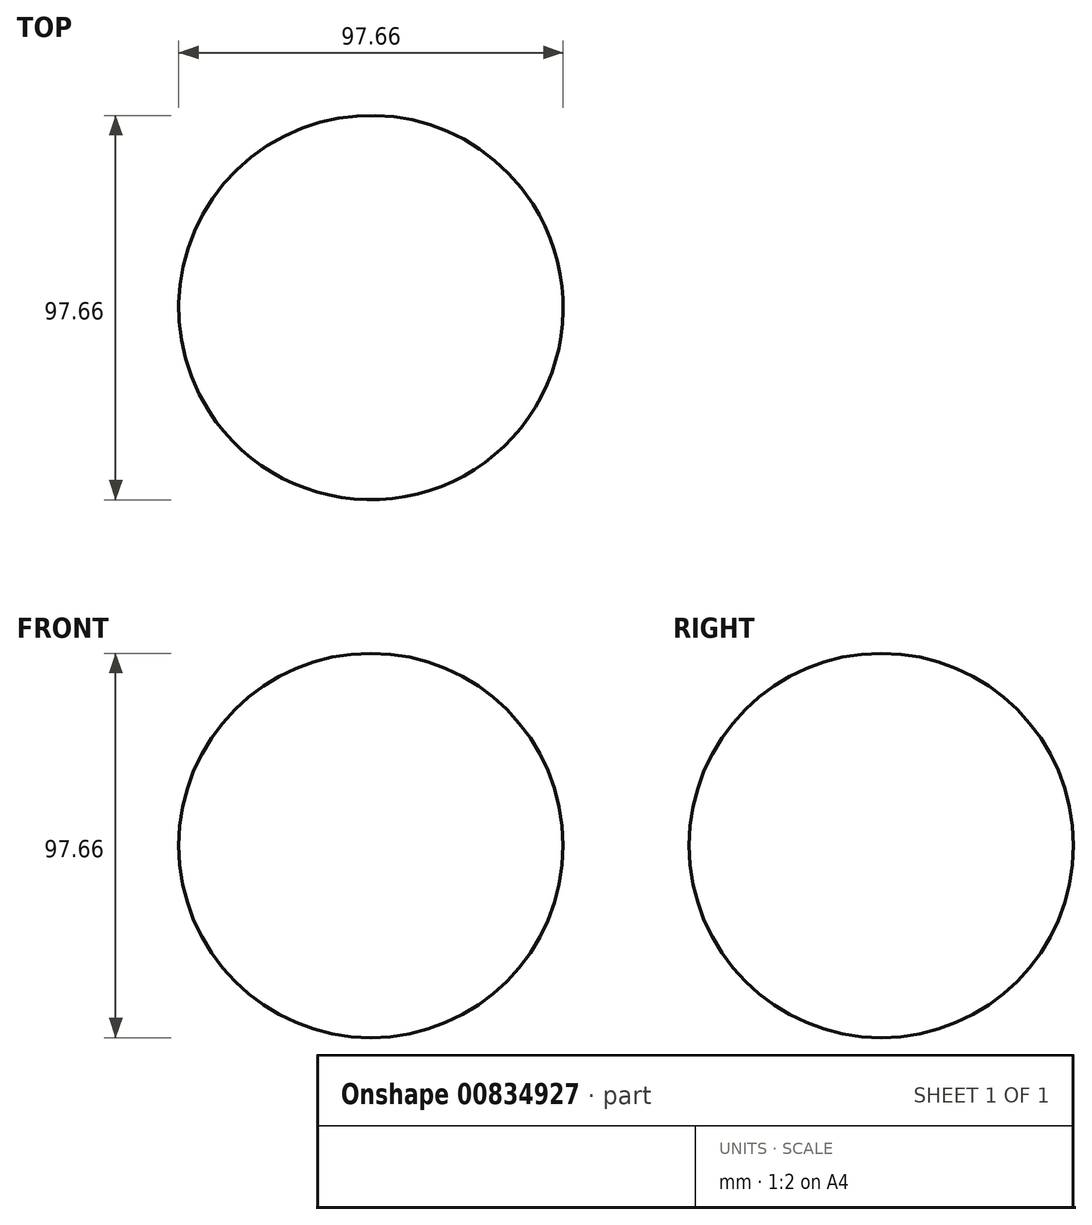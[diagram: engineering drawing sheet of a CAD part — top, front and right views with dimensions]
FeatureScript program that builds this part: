
annotation { "Feature Type Name" : "Feature", "Feature Type Description" : "" }
export const myFeature = defineFeature(function(context is Context, id is Id, definition is map)
    precondition{}
    {
        {
            var Q0;
            Q0=qCreatedBy(makeId("Top.planeOp"),FACE);
            var sketch = newSketch(context, id + "F0", { "sketchPlane" : qUnion([Q0])});
            skArc(sketch, "E0", {"start": v(41.12, 26.33) * mm, "mid": v(-26.33, 41.12) * mm, "end": v(-41.12, -26.33) * mm});
            skLineSegment(sketch, "E1", {"start": v(41.12, 26.33) * mm, "end": v(-41.12, -26.33) * mm});
            skSolve(sketch);
        }
        {
            var Q0;
            Q0=makeQuery(id+"F0.imprint","IMPRINT",FACE,{"disambiguationData":[TD([[makeQuery(id+"F0.imprint","IMPRINT",EDGE,{"derivedFrom":sQuery(id+"F0.wireOp",EDGE,"E0")}),1.0]])]});
            var Q1;
            Q1=sQuery(id+"F0.wireOp",EDGE,"E1");
            revolve(context, id + "F1", {"surfaceOperationType" : NewSurfaceOperationType.NEW, "entities" : qUnion([Q0]), "axis" : qUnion([Q1]), "revolveType" : RevolveType.FULL});
        }
    });
